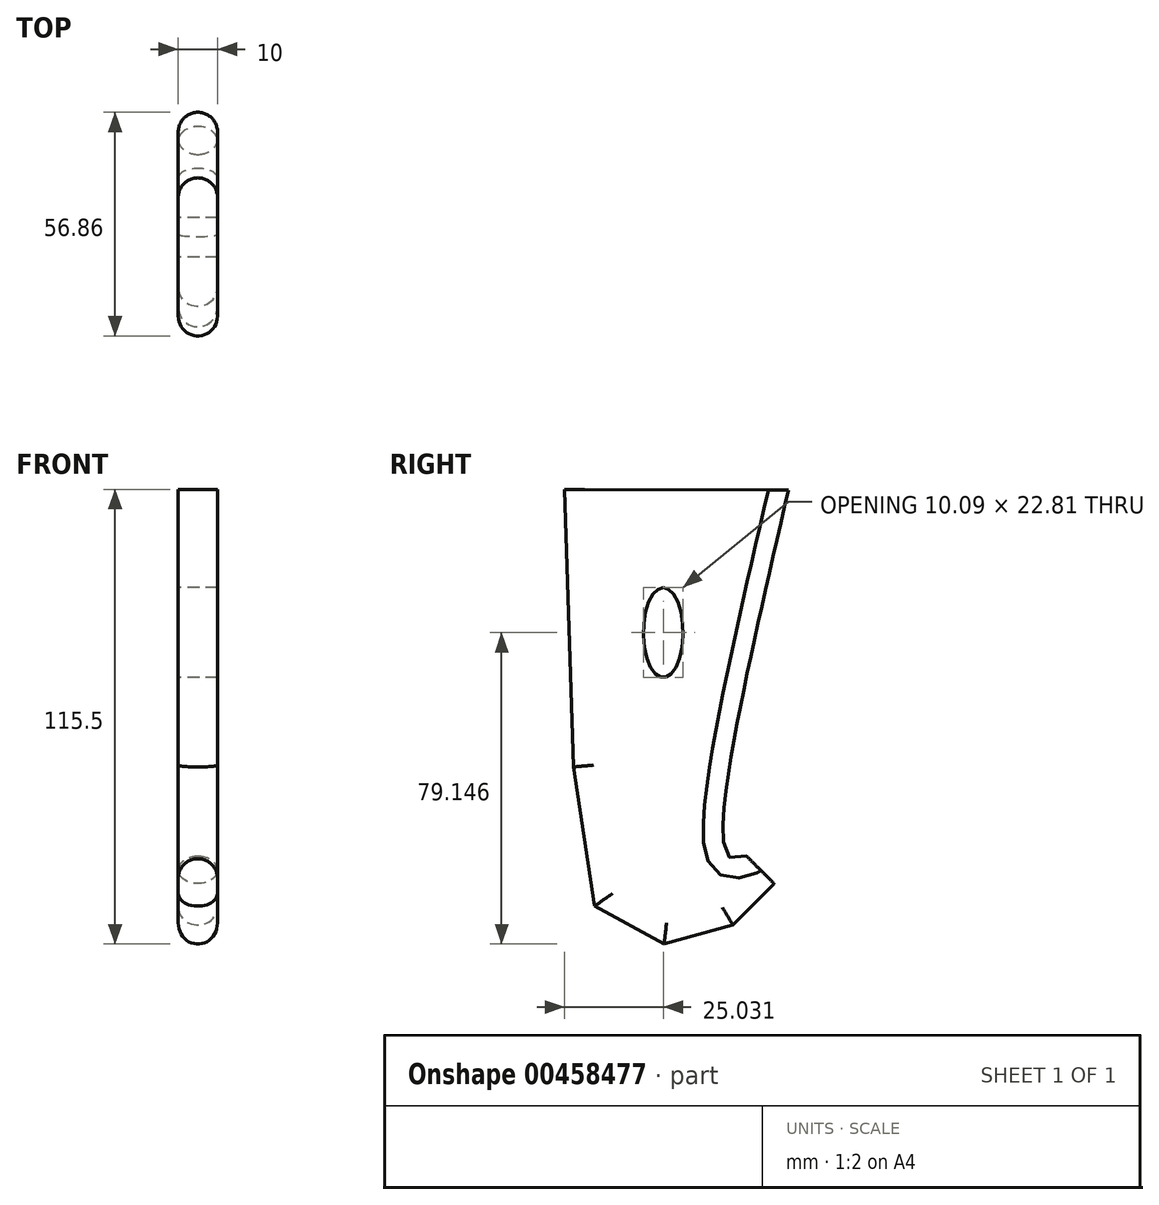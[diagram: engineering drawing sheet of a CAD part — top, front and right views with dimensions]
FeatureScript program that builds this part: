
annotation { "Feature Type Name" : "Feature", "Feature Type Description" : "" }
export const myFeature = defineFeature(function(context is Context, id is Id, definition is map)
    precondition{}
    {
        {
            var Q0;
            Q0=qCreatedBy(makeId("Top.planeOp"),FACE);
            var sketch = newSketch(context, id + "F0", { "sketchPlane" : qUnion([Q0])});
            skLineSegment(sketch, "E0.bottom", {"start": v(50, 50) * mm, "end": v(-50, 50) * mm});
            skLineSegment(sketch, "E0.top", {"start": v(50, -50) * mm, "end": v(-50, -50) * mm});
            skLineSegment(sketch, "E0.left", {"start": v(50, 50) * mm, "end": v(50, -50) * mm});
            skLineSegment(sketch, "E0.right", {"start": v(-50, 50) * mm, "end": v(-50, -50) * mm});
            skPoint(sketch, "E0.middle", {"position": v(0, 0) * mm});
            skSolve(sketch);
        }
        {
            var Q0;
            Q0=qCreatedBy(makeId("Right.planeOp"),FACE);
            var sketch = newSketch(context, id + "F1", { "sketchPlane" : qUnion([Q0])});
            skLineSegment(sketch, "E1", {"start": v(32.93, -92.93) * mm, "end": v(40, -100) * mm});
            skLineSegment(sketch, "E2", {"start": v(40, -100) * mm, "end": v(50, -100) * mm});
            skLineSegment(sketch, "E3", {"start": v(50, -100) * mm, "end": v(50, 0) * mm});
            skLineSegment(sketch, "E4", {"start": v(40, -100) * mm, "end": v(29.49, -110.51) * mm});
            skLineSegment(sketch, "E5", {"start": v(29.49, -110.51) * mm, "end": v(12.06, -115.35) * mm});
            skLineSegment(sketch, "E6", {"start": v(12.06, -115.35) * mm, "end": v(-5.63, -105.7) * mm});
            skLineSegment(sketch, "E7", {"start": v(-5.63, -105.7) * mm, "end": v(-10.9, -70.34) * mm});
            skLineSegment(sketch, "E8", {"start": v(-10.9, -70.34) * mm, "end": v(-13.2, 0.15) * mm});
            skFitSpline(sketch, "E9", {"points": [v(32.93, -92.93) * mm, v(28.21, -92.93) * mm, v(43.66, 0.05) * mm], "startDerivative": vector(-29.89, -10.4) * mm, "endDerivative": vector(37.17, 160.27) * mm});
            skLineSegment(sketch, "E10", {"start": v(43.66, 0.05) * mm, "end": v(-13.2, 0.15) * mm});
            skEllipse(sketch, "E11", {"center": v(11.83, -36.2) * mm, "majorRadius": 11.4 * mm, "minorRadius": 5.05 * mm, "majorAxis": v(0, 1)});
            skSolve(sketch);
        }
        {
            var Q0;
            Q0=makeQuery(id+"F1.imprint","IMPRINT",FACE,{"disambiguationData":[TD([[makeQuery(id+"F1.imprint","IMPRINT",EDGE,{"derivedFrom":sQuery(id+"F1.wireOp",EDGE,"E1")}),-1.0]])]});
            extrude(context, id + "F2", {"entities" : qUnion([Q0]), "endBound" : BoundingType.SYMMETRIC, "depth" : 10 * mm});
        }
        {
            var Q0;
            Q0=makeQuery(id+"F2.opExtrude","CAP_EDGE",EDGE,{"disambiguationData":[OSD([sQuery(id+"F1.wireOp",EDGE,"E9")])],"isStart":false});
            var Q1;
            Q1=makeQuery(id+"F2.opExtrude","CAP_EDGE",EDGE,{"disambiguationData":[OSD([sQuery(id+"F1.wireOp",EDGE,"E4")])],"isStart":false});
            var Q2;
            Q2=makeQuery(id+"F2.opExtrude","CAP_EDGE",EDGE,{"disambiguationData":[OSD([sQuery(id+"F1.wireOp",EDGE,"E5")])],"isStart":false});
            var Q3;
            Q3=makeQuery(id+"F2.opExtrude","CAP_EDGE",EDGE,{"disambiguationData":[OSD([sQuery(id+"F1.wireOp",EDGE,"E6")])],"isStart":false});
            var Q4;
            Q4=makeQuery(id+"F2.opExtrude","CAP_EDGE",EDGE,{"disambiguationData":[OSD([sQuery(id+"F1.wireOp",EDGE,"E7")])],"isStart":false});
            var Q5;
            Q5=makeQuery(id+"F2.opExtrude","CAP_EDGE",EDGE,{"disambiguationData":[OSD([sQuery(id+"F1.wireOp",EDGE,"E8")])],"isStart":false});
            var Q6;
            Q6=makeQuery(id+"F2.opExtrude","CAP_EDGE",EDGE,{"disambiguationData":[OSD([sQuery(id+"F1.wireOp",EDGE,"E9")])],"isStart":true});
            var Q7;
            Q7=makeQuery(id+"F2.opExtrude","CAP_EDGE",EDGE,{"disambiguationData":[OSD([sQuery(id+"F1.wireOp",EDGE,"E4")])],"isStart":true});
            var Q8;
            Q8=makeQuery(id+"F2.opExtrude","CAP_EDGE",EDGE,{"disambiguationData":[OSD([sQuery(id+"F1.wireOp",EDGE,"E5")])],"isStart":true});
            var Q9;
            Q9=makeQuery(id+"F2.opExtrude","CAP_EDGE",EDGE,{"disambiguationData":[OSD([sQuery(id+"F1.wireOp",EDGE,"E6")])],"isStart":true});
            var Q10;
            Q10=makeQuery(id+"F2.opExtrude","CAP_EDGE",EDGE,{"disambiguationData":[OSD([sQuery(id+"F1.wireOp",EDGE,"E7")])],"isStart":true});
            var Q11;
            Q11=makeQuery(id+"F2.opExtrude","CAP_EDGE",EDGE,{"disambiguationData":[OSD([sQuery(id+"F1.wireOp",EDGE,"E8")])],"isStart":true});
            fillet(context, id + "F3", {"entities" : qUnion([Q0, Q1, Q2, Q3, Q4, Q5, Q6, Q7, Q8, Q9, Q10, Q11]), "radius" : 5 * mm, "tangentPropagation" : true, "allowEdgeOverflow" : false});
        }
    });
